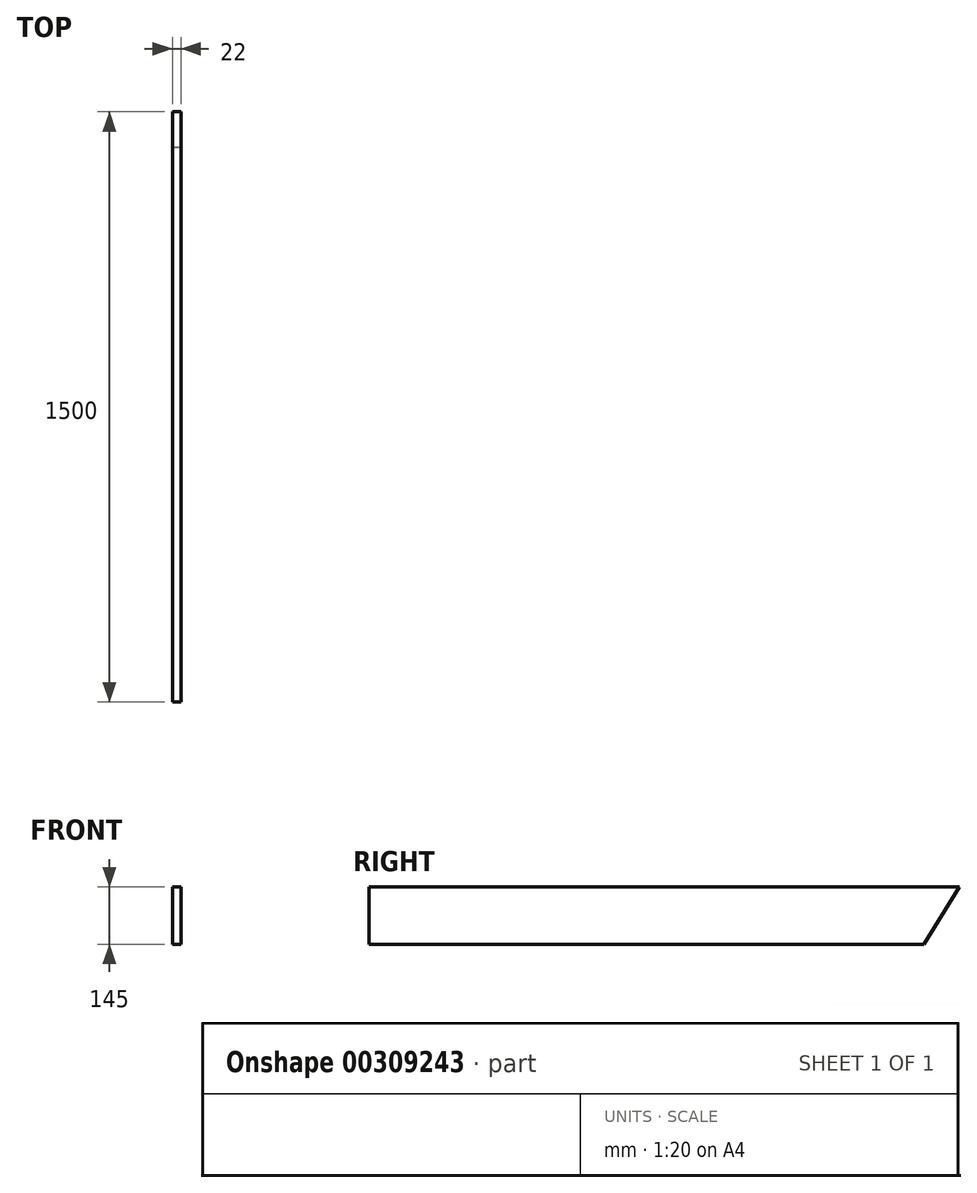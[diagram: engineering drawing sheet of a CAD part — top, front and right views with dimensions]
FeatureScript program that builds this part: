
annotation { "Feature Type Name" : "Feature", "Feature Type Description" : "" }
export const myFeature = defineFeature(function(context is Context, id is Id, definition is map)
    precondition{}
    {
        {
            var Q0;
            Q0=qCreatedBy(makeId("Right.planeOp"),FACE);
            var sketch = newSketch(context, id + "F0", { "sketchPlane" : qUnion([Q0])});
            skLineSegment(sketch, "E0.bottom", {"start": v(0, 0) * mm, "end": v(1500, 0) * mm});
            skLineSegment(sketch, "E0.top", {"start": v(0, 145) * mm, "end": v(1500, 145) * mm});
            skLineSegment(sketch, "E0.left", {"start": v(0, 0) * mm, "end": v(0, 145) * mm});
            skLineSegment(sketch, "E0.right", {"start": v(1500, 0) * mm, "end": v(1500, 145) * mm});
            skSolve(sketch);
        }
        {
            var Q0;
            Q0 = qSketchRegion(id + "F0", true);
            extrude(context, id + "F1", {"entities" : qUnion([Q0]), "depth" : 22 * mm});
        }
        {
            var Q0;
            Q0=makeQuery(id+"F1.opExtrude","CAP_FACE",FACE,{"disambiguationData":[OSD([sQuery(id+"F0.wireOp",EDGE,"E0.bottom"),sQuery(id+"F0.wireOp",EDGE,"E0.top"),sQuery(id+"F0.wireOp",EDGE,"E0.left"),sQuery(id+"F0.wireOp",EDGE,"E0.right")])],"isStart":false});
            var sketch = newSketch(context, id + "F2", { "sketchPlane" : qUnion([Q0])});
            skLineSegment(sketch, "E1", {"start": v(1500, 145) * mm, "end": v(1395.99, -22.83) * mm});
            skLineSegment(sketch, "E2", {"start": v(1395.99, -22.83) * mm, "end": v(1500, -22.83) * mm});
            skLineSegment(sketch, "E3", {"start": v(1500, -22.83) * mm, "end": v(1500, 145) * mm});
            skSolve(sketch);
        }
        {
            var Q0;
            {var subQ0=sQuery(id+"F2.wireOp",EDGE,"E2");Q0=makeQuery(id+"F2.imprint","IMPRINT",FACE,{"disambiguationData":[TD([[makeQuery(id+"F2.imprint","IMPRINT",EDGE,{"derivedFrom":subQ0}),1.0]])]});}
            var Q1;
            {var subQ0=sQuery(id+"F2.wireOp",EDGE,"E3");var subQ3=makeQuery(id+"F1.opExtrude","CAP_EDGE",EDGE,{"disambiguationData":[OSD([sQuery(id+"F0.wireOp",EDGE,"E0.bottom")])],"isStart":false});var subQ5=makeQuery(id+"F2.imprint","INTERSECT",VERTEX,{"derivedFrom":[subQ3,subQ0]});Q1=makeQuery(id+"F2.imprint","IMPRINT",FACE,{"disambiguationData":[TD([[makeQuery(id+"F2.imprint","IMPRINT",EDGE,{"disambiguationData":[TD([[subQ5,1.0]])],"derivedFrom":subQ3}),1.0]])]});}
            extrude(context, id + "F3", {"entities" : qUnion([Q0, Q1]), "operationType" : NewBodyOperationType.REMOVE, "oppositeDirection" : true, "depth" : 25 * mm});
        }
    });
